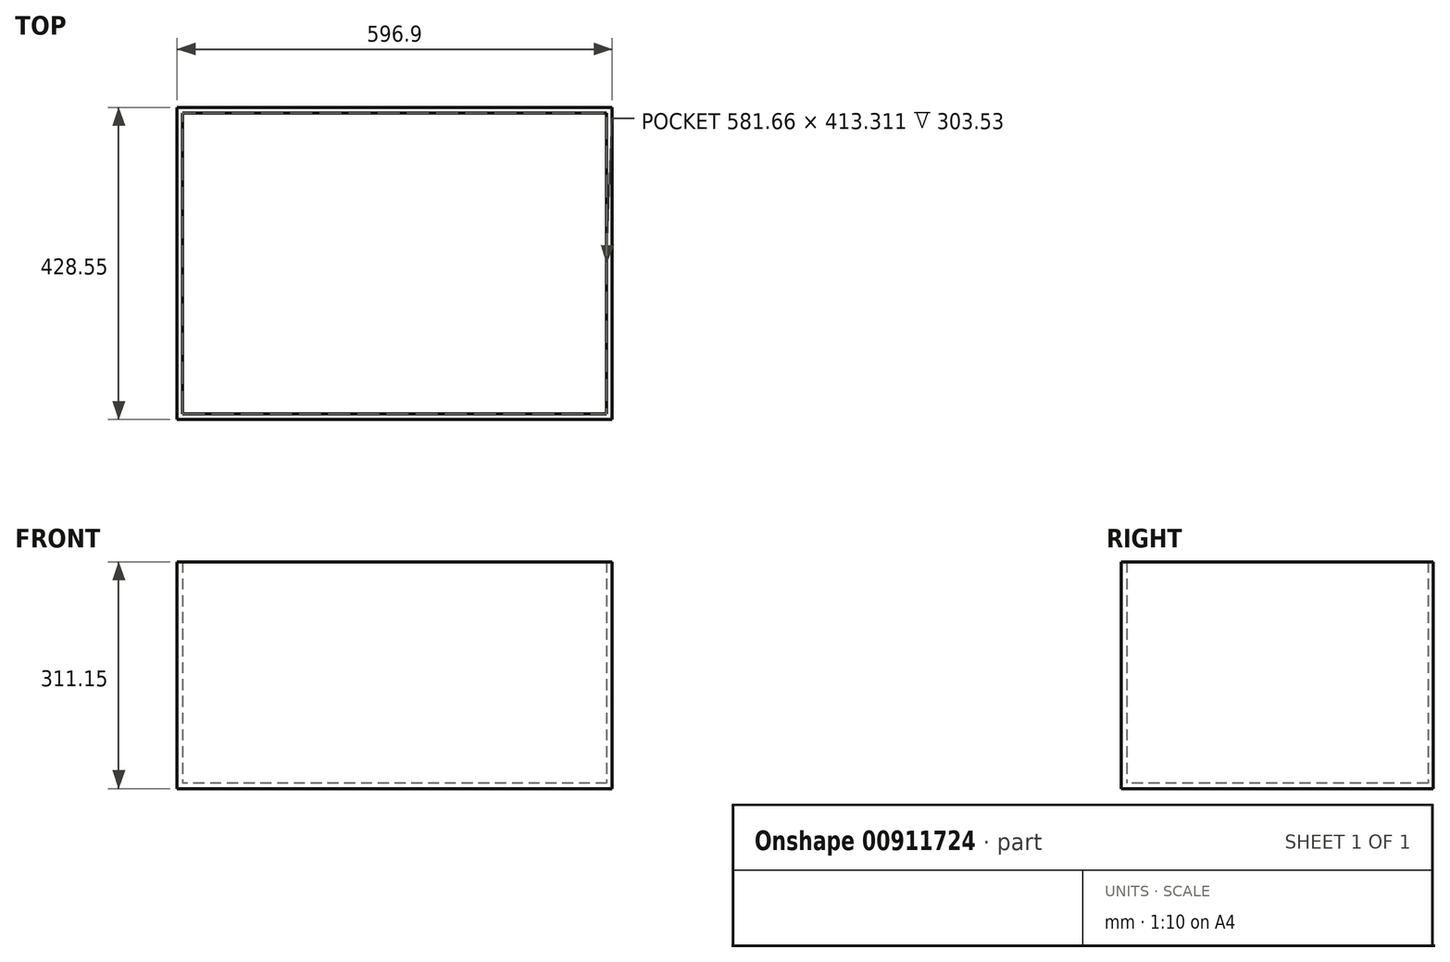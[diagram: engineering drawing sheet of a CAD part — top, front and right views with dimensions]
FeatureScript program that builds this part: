
annotation { "Feature Type Name" : "Feature", "Feature Type Description" : "" }
export const myFeature = defineFeature(function(context is Context, id is Id, definition is map)
    precondition{}
    {
        {
            var Q0;
            Q0=qCreatedBy(makeId("Top.planeOp"),FACE);
            var sketch = newSketch(context, id + "F0", { "sketchPlane" : qUnion([Q0])});
            skLineSegment(sketch, "E0", {"start": v(342.24, 173.46) * mm, "end": v(-254.66, 173.46) * mm});
            skLineSegment(sketch, "E1", {"start": v(334.3, -255.1) * mm, "end": v(-254.66, -255.1) * mm});
            skLineSegment(sketch, "E2", {"start": v(-254.66, 173.46) * mm, "end": v(-254.66, -197.85) * mm});
            skLineSegment(sketch, "E3", {"start": v(-254.66, -197.85) * mm, "end": v(-254.66, -255.1) * mm});
            skLineSegment(sketch, "E4", {"start": v(342.24, 173.46) * mm, "end": v(342.24, -255.1) * mm});
            skLineSegment(sketch, "E5", {"start": v(342.24, -255.1) * mm, "end": v(334.3, -255.1) * mm});
            skPoint(sketch, "E6.orphan", {"position": v(-262.6, -255.1) * mm});
            skSolve(sketch);
        }
        {
            var Q0;
            Q0=makeQuery(id+"F0.imprint","IMPRINT",FACE,{"disambiguationData":[TD([[makeQuery(id+"F0.imprint","IMPRINT",EDGE,{"derivedFrom":sQuery(id+"F0.wireOp",EDGE,"edPnhqVf-zbbV-1j8M-V0QE-Wjehic2dlwdW.bottom")}),1.0]])]});
            var Q1;
            Q1=makeQuery(id+"F0.imprint","IMPRINT",FACE,{"disambiguationData":[TD([[makeQuery(id+"F0.imprint","IMPRINT",EDGE,{"derivedFrom":sQuery(id+"F0.wireOp",EDGE,"E0")}),1.0]])]});
            extrude(context, id + "F1", {"entities" : qUnion([Q0, Q1]), "depth" : 311.15 * mm, "offsetDistance" : 25.4 * mm});
        }
        {
            var Q0;
            Q0=makeQuery(id+"F1.opExtrude","CAP_FACE",FACE,{"disambiguationData":[OSD([sQuery(id+"F0.wireOp",EDGE,"edPnhqVf-zbbV-1j8M-V0QE-Wjehic2dlwdW.bottom"),sQuery(id+"F0.wireOp",EDGE,"edPnhqVf-zbbV-1j8M-V0QE-Wjehic2dlwdW.top"),sQuery(id+"F0.wireOp",EDGE,"edPnhqVf-zbbV-1j8M-V0QE-Wjehic2dlwdW.left"),sQuery(id+"F0.wireOp",EDGE,"edPnhqVf-zbbV-1j8M-V0QE-Wjehic2dlwdW.right")])],"isStart":false});
            var Q1;
            Q1=makeQuery(id+"F1.opExtrude","CAP_FACE",FACE,{"disambiguationData":[OSD([sQuery(id+"F0.wireOp",EDGE,"E0"),sQuery(id+"F0.wireOp",EDGE,"E1"),sQuery(id+"F0.wireOp",EDGE,"E2"),sQuery(id+"F0.wireOp",EDGE,"E3"),sQuery(id+"F0.wireOp",EDGE,"E4"),sQuery(id+"F0.wireOp",EDGE,"E5")])],"isStart":false});
            shell(context, id + "F2", {"entities" : qUnion([Q0, Q1]), "thickness" : 7.62 * mm});
        }
    });
